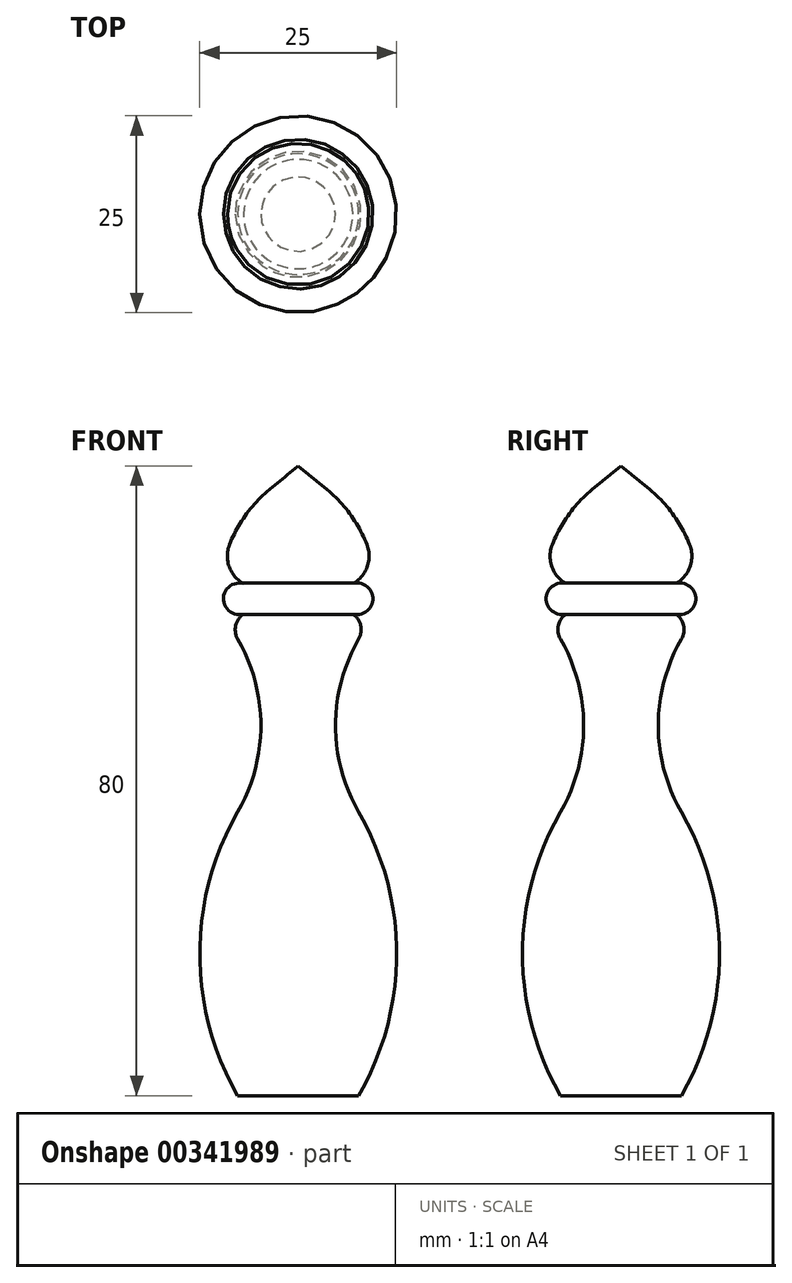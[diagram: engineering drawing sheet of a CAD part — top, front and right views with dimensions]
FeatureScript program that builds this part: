
annotation { "Feature Type Name" : "Feature", "Feature Type Description" : "" }
export const myFeature = defineFeature(function(context is Context, id is Id, definition is map)
    precondition{}
    {
        {
            var Q0;
            Q0=qCreatedBy(makeId("Front.planeOp"),FACE);
            var sketch = newSketch(context, id + "F0", { "sketchPlane" : qUnion([Q0])});
            skArc(sketch, "E0", {"start": v(6.94, -18.78) * mm, "mid": v(9.5, -16.86) * mm, "end": v(6.94, -14.94) * mm});
            skArc(sketch, "E1", {"start": v(7.68, -22) * mm, "mid": v(7.94, -20.25) * mm, "end": v(6.94, -18.78) * mm});
            skArc(sketch, "E2", {"start": v(7.68, -22) * mm, "mid": v(4.74, -32.97) * mm, "end": v(7.68, -43.94) * mm});
            skArc(sketch, "E3", {"start": v(7.68, -80) * mm, "mid": v(12.5, -61.97) * mm, "end": v(7.68, -43.94) * mm});
            skLineSegment(sketch, "E4", {"start": v(7.68, -80) * mm, "end": v(0, -80) * mm});
            skLineSegment(sketch, "E5", {"start": v(0, -80) * mm, "end": v(0, 0) * mm});
            skLineSegment(sketch, "E6", {"start": v(0, 0) * mm, "end": v(3.66, -3) * mm});
            skArc(sketch, "E7", {"start": v(6.94, -14.94) * mm, "mid": v(8.76, -12.8) * mm, "end": v(8.73, -10) * mm});
            skArc(sketch, "E8", {"start": v(8.73, -10) * mm, "mid": v(6.65, -6.17) * mm, "end": v(3.66, -3) * mm});
            skSolve(sketch);
        }
        {
            var Q0;
            Q0=makeQuery(id+"F0.imprint","IMPRINT",FACE,{"disambiguationData":[TD([[makeQuery(id+"F0.imprint","IMPRINT",EDGE,{"derivedFrom":sQuery(id+"F0.wireOp",EDGE,"E0")}),1.0]])]});
            var Q1;
            Q1=sQuery(id+"F0.wireOp",EDGE,"E5");
            revolve(context, id + "F1", {"entities" : qUnion([Q0]), "axis" : qUnion([Q1]), "revolveType" : RevolveType.FULL});
        }
    });
